# Revit family: LHA4
name_source: partatom
category: Lighting Fixtures
revit_build: Autodesk Revit Architecture 2012 (Build: 20110309_2315(x64)
units: mm (PartAtom-declared; Revit-internal decimal feet)

## types (6) — shared parameters
Apparent Load = 0 VA
Backbox = White
Color Filter = 16777215
Default Elevation = 48.000"
Description = LHA high bays are the economical standard for fluorescent high bay lighting with serviceability and performance that is unrivaled in the marketplace.
Dimming Lamp Color Temperature Shift = <None>
Emit from Line Length = 48.000"
Glass = Glass
Lamp = F54T5
Manufacturer = Columbia Lighting
Manufacturer Fax = 866-898-1065
Model = LHA4
Product Documentation Link = http://www.columbialighting.com
Product Page URL = http://www.columbialighting.com
Tilt Angle = -90.00°
URL = http://www.columbialighting.com
Wattage Comments = 235W

## per-type parameters (varying)
| type | Photometric Web File |
| LHA4-454-NU-4EP | itl68013.ies |
| LHA4-454-WU | 15332.ies |
| LHA4-632-NU-EHL | itl68009.ies |
| LHA4-632-WU | 15333.ies |
| LHA4-654-NU-24EP | itl68011.ies |
| LHA4-654-WU | 15334.ies |

## geometry (parser evidence)
native form markers: Sweep x1
no freeform markers — native parametric forms only
